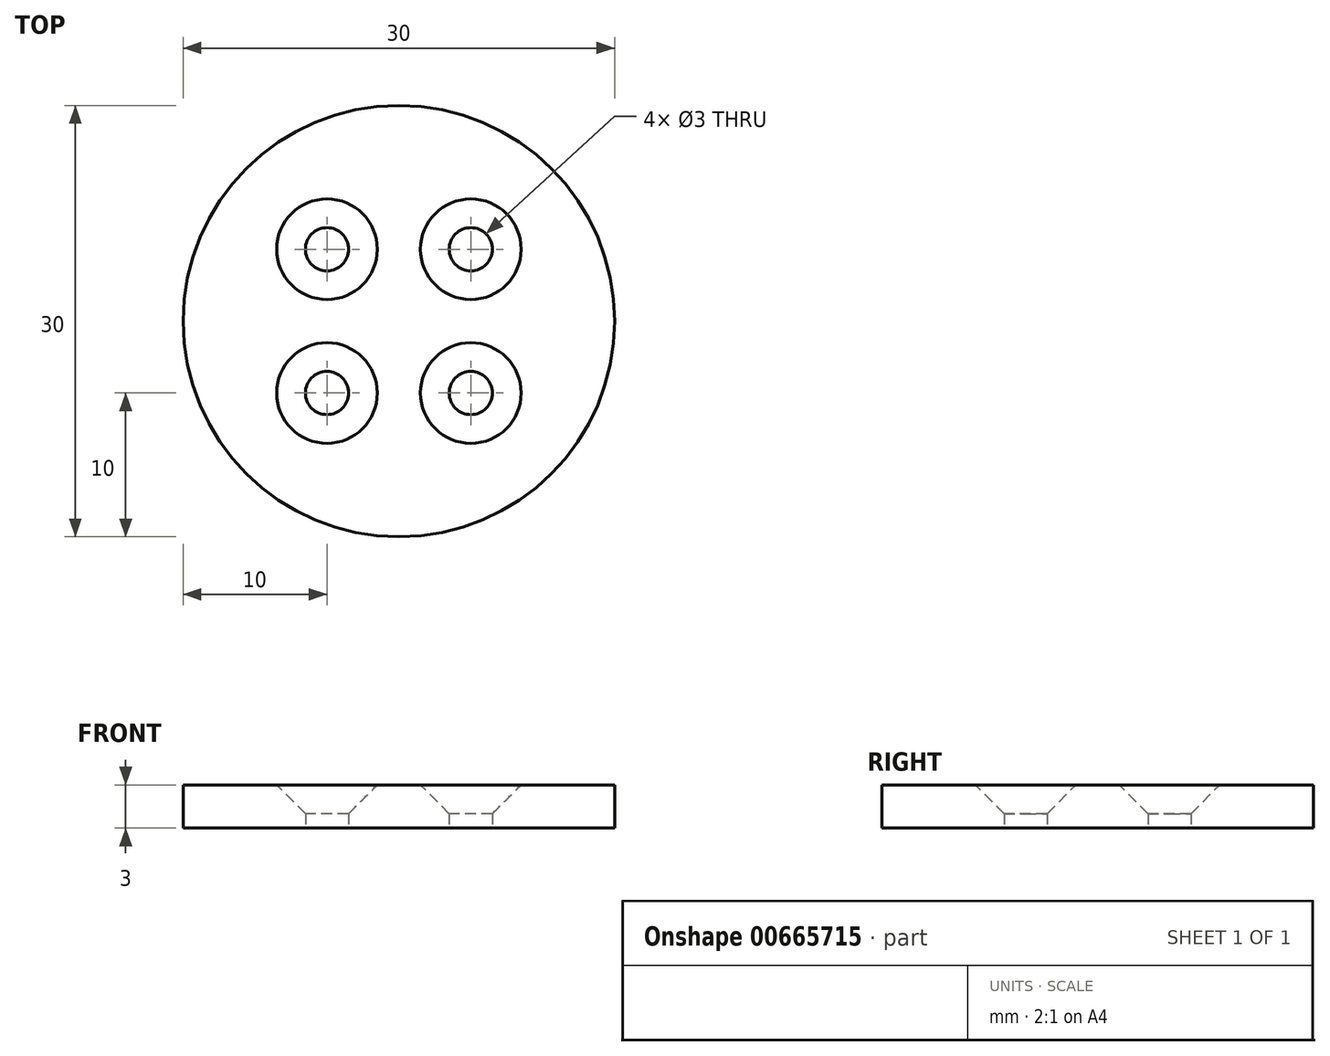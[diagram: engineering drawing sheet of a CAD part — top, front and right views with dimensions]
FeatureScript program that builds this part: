
annotation { "Feature Type Name" : "Feature", "Feature Type Description" : "" }
export const myFeature = defineFeature(function(context is Context, id is Id, definition is map)
    precondition{}
    {
        {
            var Q0;
            Q0=qCreatedBy(makeId("Top.planeOp"),FACE);
            var sketch = newSketch(context, id + "F0", { "sketchPlane" : qUnion([Q0])});
            skCircle(sketch, "E0", {"center": v(0, 0) * mm, "radius": 12.5 * mm});
            skCircle(sketch, "E1", {"center": v(0, 0) * mm, "radius": 23.5 * mm});
            skLineSegment(sketch, "E2.bottom", {"start": v(36.5, -36.5) * mm, "end": v(-36.5, -36.5) * mm});
            skLineSegment(sketch, "E2.top", {"start": v(36.5, 36.5) * mm, "end": v(-36.5, 36.5) * mm});
            skLineSegment(sketch, "E2.left", {"start": v(36.5, -36.5) * mm, "end": v(36.5, 36.5) * mm});
            skLineSegment(sketch, "E2.right", {"start": v(-36.5, -36.5) * mm, "end": v(-36.5, 36.5) * mm});
            skLineSegment(sketch, "E3.bottom", {"start": v(28.5, -28.5) * mm, "end": v(-28.5, -28.5) * mm});
            skLineSegment(sketch, "E3.top", {"start": v(28.5, 28.5) * mm, "end": v(-28.5, 28.5) * mm});
            skLineSegment(sketch, "E3.left", {"start": v(28.5, -28.5) * mm, "end": v(28.5, 28.5) * mm});
            skLineSegment(sketch, "E3.right", {"start": v(-28.5, -28.5) * mm, "end": v(-28.5, 28.5) * mm});
            skCircle(sketch, "E4", {"center": v(-28.5, 28.5) * mm, "radius": 3 * mm});
            skCircle(sketch, "E5", {"center": v(28.5, 28.5) * mm, "radius": 3 * mm});
            skCircle(sketch, "E6", {"center": v(28.5, -28.5) * mm, "radius": 3 * mm});
            skCircle(sketch, "E7", {"center": v(-28.5, -28.5) * mm, "radius": 3 * mm});
            skCircle(sketch, "E8", {"center": v(0, 0) * mm, "radius": 17.5 * mm});
            skCircle(sketch, "E9", {"center": v(0, 0) * mm, "radius": 15 * mm});
            skCircle(sketch, "E10", {"center": v(-28.5, 28.5) * mm, "radius": 8 * mm});
            skCircle(sketch, "E11", {"center": v(28.5, 28.5) * mm, "radius": 8 * mm});
            skCircle(sketch, "E12", {"center": v(28.5, -28.5) * mm, "radius": 8 * mm});
            skCircle(sketch, "E13", {"center": v(-28.5, -28.5) * mm, "radius": 8 * mm});
            skLineSegment(sketch, "E14.bottom", {"start": v(5, -5) * mm, "end": v(-5, -5) * mm});
            skLineSegment(sketch, "E14.top", {"start": v(5, 5) * mm, "end": v(-5, 5) * mm});
            skLineSegment(sketch, "E14.left", {"start": v(5, -5) * mm, "end": v(5, 5) * mm});
            skLineSegment(sketch, "E14.right", {"start": v(-5, -5) * mm, "end": v(-5, 5) * mm});
            skCircle(sketch, "E15", {"center": v(-5, 5) * mm, "radius": 1.5 * mm});
            skCircle(sketch, "E16", {"center": v(5, 5) * mm, "radius": 1.5 * mm});
            skCircle(sketch, "E17", {"center": v(5, -5) * mm, "radius": 1.5 * mm});
            skCircle(sketch, "E18", {"center": v(-5, -5) * mm, "radius": 1.5 * mm});
            skSolve(sketch);
        }
        {
            var Q0;
            Q0=makeQuery(id+"F0.imprint","IMPRINT",FACE,{"disambiguationData":[TD([[makeQuery(id+"F0.imprint","IMPRINT",EDGE,{"derivedFrom":sQuery(id+"F0.wireOp",EDGE,"E0")}),-1.0]])]});
            var Q1;
            Q1=makeQuery(id+"F0.imprint","IMPRINT",FACE,{"disambiguationData":[TD([[makeQuery(id+"F0.imprint","IMPRINT",EDGE,{"derivedFrom":sQuery(id+"F0.wireOp",EDGE,"E0")}),1.0]])]});
            var Q2;
            {var subQ5=sQuery(id+"F0.wireOp",EDGE,"E17");var subQ10=sQuery(id+"F0.wireOp",EDGE,"E14.bottom");var subQ15=makeQuery(id+"F0.imprint","INTERSECT",VERTEX,{"derivedFrom":[subQ10,subQ5]});Q2=makeQuery(id+"F0.imprint","IMPRINT",FACE,{"disambiguationData":[TD([[makeQuery(id+"F0.imprint","IMPRINT",EDGE,{"disambiguationData":[TD([[subQ15,-1.0]])],"derivedFrom":subQ10}),-1.0]])]});}
            extrude(context, id + "F1", {"entities" : qUnion([Q0, Q1, Q2]), "depth" : 3 * mm, "offsetDistance" : 25 * mm});
        }
        {
            var Q0;
            Q0=makeQuery(id+"F1.opExtrude","CAP_EDGE",EDGE,{"disambiguationData":[OSD([sQuery(id+"F0.wireOp",EDGE,"E15")])],"isStart":false});
            var Q1;
            Q1=makeQuery(id+"F1.opExtrude","CAP_EDGE",EDGE,{"disambiguationData":[OSD([sQuery(id+"F0.wireOp",EDGE,"E16")])],"isStart":false});
            var Q2;
            Q2=makeQuery(id+"F1.opExtrude","CAP_EDGE",EDGE,{"disambiguationData":[OSD([sQuery(id+"F0.wireOp",EDGE,"E18")])],"isStart":false});
            var Q3;
            Q3=makeQuery(id+"F1.opExtrude","CAP_EDGE",EDGE,{"disambiguationData":[OSD([sQuery(id+"F0.wireOp",EDGE,"E17")])],"isStart":false});
            chamfer(context, id + "F2", {"entities" : qUnion([Q0, Q1, Q2, Q3]), "width" : 2 * mm, "tangentPropagation" : true});
        }
    });
